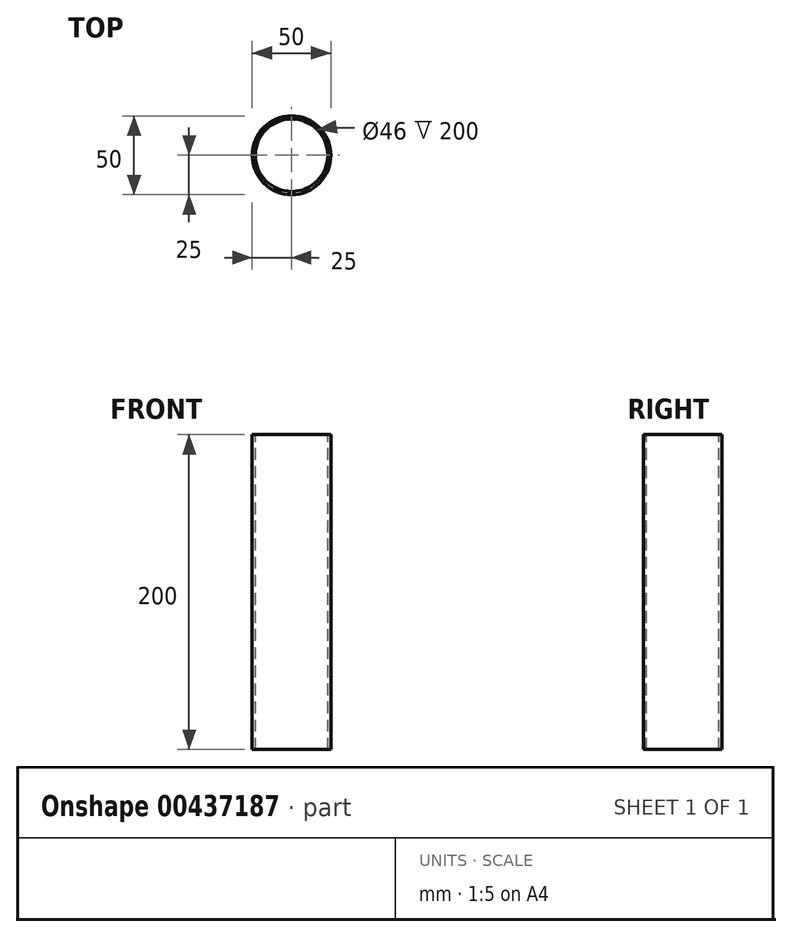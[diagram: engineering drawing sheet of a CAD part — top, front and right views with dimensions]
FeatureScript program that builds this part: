
annotation { "Feature Type Name" : "Feature", "Feature Type Description" : "" }
export const myFeature = defineFeature(function(context is Context, id is Id, definition is map)
    precondition{}
    {
        {
            var Q0;
            Q0=qCreatedBy(makeId("Top.planeOp"),FACE);
            var sketch = newSketch(context, id + "F0", { "sketchPlane" : qUnion([Q0])});
            skCircle(sketch, "E0", {"center": v(0, 0) * mm, "radius": 25 * mm});
            skCircle(sketch, "E1", {"center": v(0, 0) * mm, "radius": 23 * mm});
            skSolve(sketch);
        }
        {
            var Q0;
            Q0=makeQuery(id+"F0.imprint","IMPRINT",FACE,{"disambiguationData":[TD([[makeQuery(id+"F0.imprint","IMPRINT",EDGE,{"derivedFrom":sQuery(id+"F0.wireOp",EDGE,"E0")}),1.0]])]});
            extrude(context, id + "F1", {"entities" : qUnion([Q0]), "oppositeDirection" : true, "depth" : 200 * mm});
        }
    });
